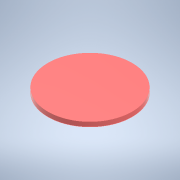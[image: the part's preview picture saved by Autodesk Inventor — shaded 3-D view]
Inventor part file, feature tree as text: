
AUTODESK INVENTOR PART (.ipt)
format: ipt  version: 2021 (Build 250183000, 183)  size: 112,128 bytes
history: native  units: mm
features: extrude x1, sketch x1
ambient origin geometry x8: Origin, YZ Plane, XZ Plane, XY Plane, X Axis, Y Axis, Z Axis, Center Point
bodies: Solid1 (feature_tree)
feature tree (2):
  extrude  "Extrusion1"  Depth=1.75mm TaperAngle=0.0deg
  sketch  "Sketch1"  dims[d0=31.7mm d1=1.75mm d2=0.0mm]
